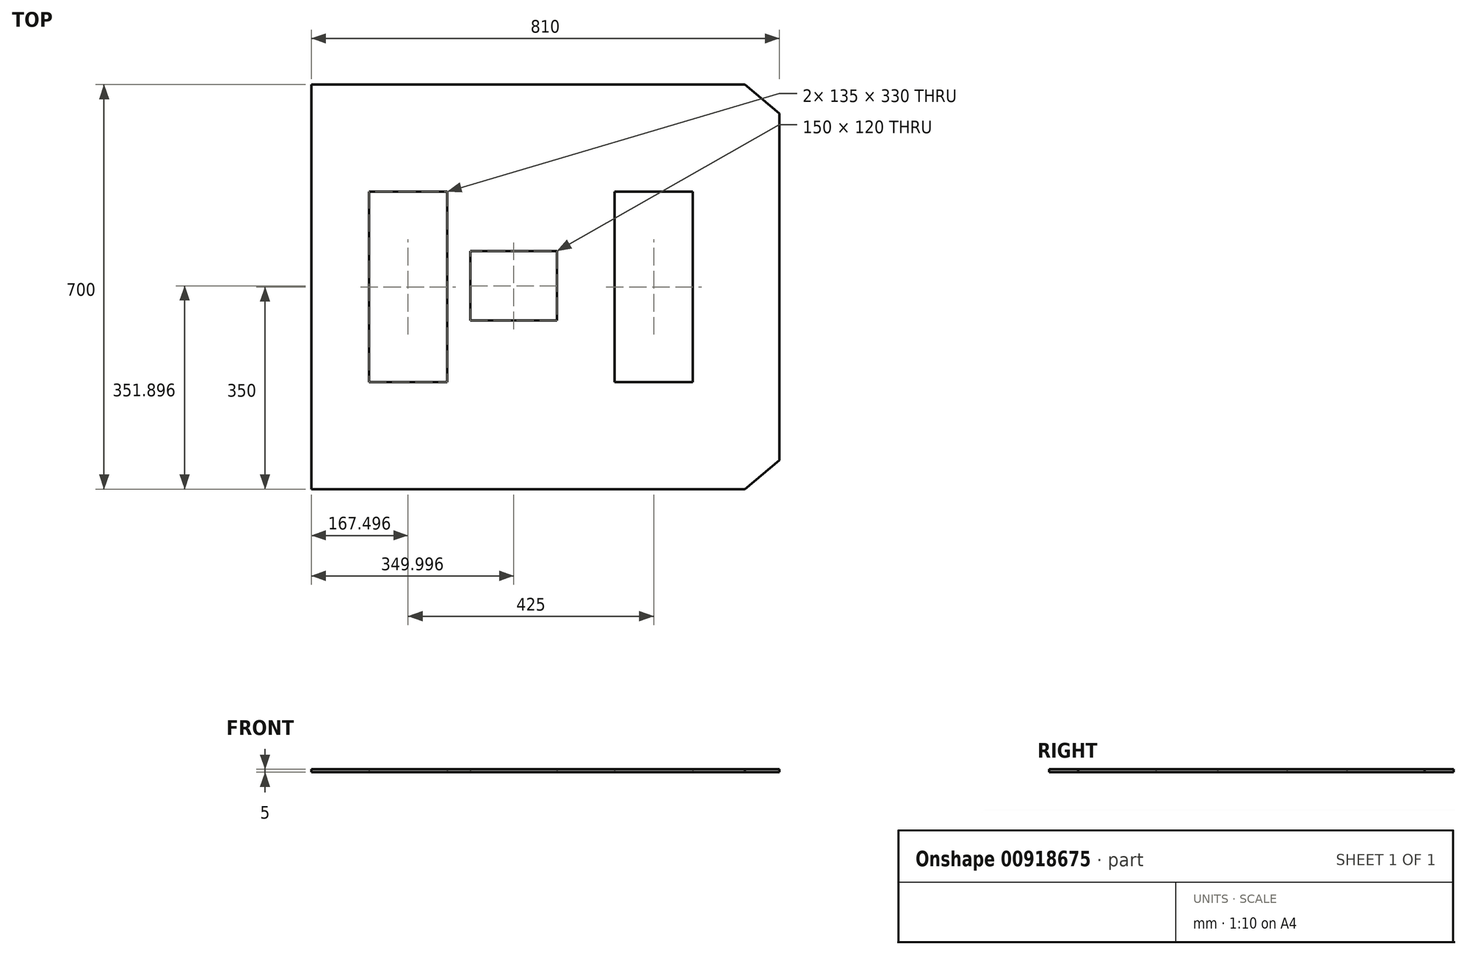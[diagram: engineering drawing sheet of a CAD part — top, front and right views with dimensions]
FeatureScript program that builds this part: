
annotation { "Feature Type Name" : "Feature", "Feature Type Description" : "" }
export const myFeature = defineFeature(function(context is Context, id is Id, definition is map)
    precondition{}
    {
        {
            var Q0;
            Q0=qCreatedBy(makeId("Front.planeOp"),FACE);
            var sketch = newSketch(context, id + "F0", { "sketchPlane" : qUnion([Q0])});
            skLineSegment(sketch, "E0", {"start": v(-514.8, 0) * mm, "end": v(635.2, 0) * mm, "construction": true});
            skLineSegment(sketch, "E1", {"start": v(-514.8, 0) * mm, "end": v(-514.8, 380) * mm, "construction": true});
            skCircle(sketch, "E2", {"center": v(-324.8, 190) * mm, "radius": 190 * mm, "construction": true});
            skPoint(sketch, "E2.first.point", {"position": v(-324.8, 0) * mm});
            skPoint(sketch, "E2.second.point", {"position": v(-514.8, 190) * mm});
            skPoint(sketch, "E2.third.point", {"position": v(-205.57, 337.94) * mm});
            skLineSegment(sketch, "E3", {"start": v(-514.8, 380) * mm, "end": v(635.2, 380) * mm, "construction": true});
            skLineSegment(sketch, "E4", {"start": v(635.2, 380) * mm, "end": v(635.2, 0) * mm, "construction": true});
            skCircle(sketch, "E5", {"center": v(445.2, 190) * mm, "radius": 190 * mm, "construction": true});
            skLineSegment(sketch, "E6", {"start": v(-134.8, 380) * mm, "end": v(-134.8, 0) * mm, "construction": true});
            skLineSegment(sketch, "E7", {"start": v(255.2, 380) * mm, "end": v(255.2, 0) * mm, "construction": true});
            skLineSegment(sketch, "E8", {"start": v(-542.2, 180) * mm, "end": v(670.63, 180) * mm, "construction": true});
            skLineSegment(sketch, "E9", {"start": v(-324.8, 408.83) * mm, "end": v(-324.8, -37.63) * mm, "construction": true});
            skLineSegment(sketch, "E10", {"start": v(445.2, 408.83) * mm, "end": v(445.2, -37.63) * mm, "construction": true});
            skLineSegment(sketch, "E11", {"start": v(294.65, 0) * mm, "end": v(294.65, 40) * mm, "construction": true});
            skLineSegment(sketch, "E12", {"start": v(294.65, 40) * mm, "end": v(635.2, 40) * mm, "construction": true});
            skSolve(sketch);
        }
        {
            var Q0;
            Q0=qCreatedBy(makeId("Top.planeOp"),FACE);
            var sketch = newSketch(context, id + "F1", { "sketchPlane" : qUnion([Q0])});
            skLineSegment(sketch, "E13", {"start": v(-514.8, 480) * mm, "end": v(-514.8, -480) * mm, "construction": true});
            skLineSegment(sketch, "E14", {"start": v(-134.8, 480) * mm, "end": v(-134.8, -480) * mm, "construction": true});
            skLineSegment(sketch, "E15", {"start": v(255.2, 480) * mm, "end": v(255.2, -480) * mm, "construction": true});
            skLineSegment(sketch, "E16", {"start": v(635.2, 480) * mm, "end": v(635.2, -480) * mm, "construction": true});
            skLineSegment(sketch, "E17", {"start": v(-514.8, 350) * mm, "end": v(125.2, 350) * mm, "construction": true});
            skLineSegment(sketch, "E18", {"start": v(-514.8, -350) * mm, "end": v(125.2, -350) * mm, "construction": true});
            skLineSegment(sketch, "E19", {"start": v(485.2, 180) * mm, "end": v(485.2, 0) * mm, "construction": true});
            skLineSegment(sketch, "E20", {"start": v(485.2, 0) * mm, "end": v(485.2, -180) * mm, "construction": true});
            skLineSegment(sketch, "E21", {"start": v(-514.8, 480) * mm, "end": v(635.2, 480) * mm, "construction": true});
            skLineSegment(sketch, "E22", {"start": v(-514.8, -480) * mm, "end": v(635.2, -480) * mm, "construction": true});
            skLineSegment(sketch, "E23", {"start": v(125.2, -350) * mm, "end": v(125.2, -350) * mm});
            skLineSegment(sketch, "E24", {"start": v(125.2, -350) * mm, "end": v(295.2, -350) * mm, "construction": true});
            skLineSegment(sketch, "E25", {"start": v(295.2, -350) * mm, "end": v(295.2, -235) * mm, "construction": true});
            skLineSegment(sketch, "E26", {"start": v(295.2, -235) * mm, "end": v(395.2, -235) * mm, "construction": true});
            skLineSegment(sketch, "E27", {"start": v(395.2, -235) * mm, "end": v(395.2, -180) * mm, "construction": true});
            skLineSegment(sketch, "E28", {"start": v(395.2, -180) * mm, "end": v(485.2, -180) * mm, "construction": true});
            skLineSegment(sketch, "E29", {"start": v(125.2, 350) * mm, "end": v(295.2, 350) * mm, "construction": true});
            skLineSegment(sketch, "E30.MirrorCS", {"start": v(125.2, 350) * mm, "end": v(125.2, 350) * mm});
            skLineSegment(sketch, "E31.MirrorCS", {"start": v(295.2, 350) * mm, "end": v(295.2, 235) * mm, "construction": true});
            skLineSegment(sketch, "E32.MirrorCS", {"start": v(295.2, 235) * mm, "end": v(395.2, 235) * mm, "construction": true});
            skLineSegment(sketch, "E33.MirrorCS", {"start": v(395.2, 235) * mm, "end": v(395.2, 180) * mm, "construction": true});
            skLineSegment(sketch, "E34.MirrorCS", {"start": v(395.2, 180) * mm, "end": v(485.2, 180) * mm, "construction": true});
            skLineSegment(sketch, "E35", {"start": v(295.2, 235) * mm, "end": v(295.2, -235) * mm, "construction": true});
            skSolve(sketch);
        }
        {
            var Q0;
            Q0=qCreatedBy(makeId("Front.planeOp"),FACE);
            var sketch = newSketch(context, id + "F2", { "sketchPlane" : qUnion([Q0])});
            skCircle(sketch, "E36", {"center": v(-214.8, 300) * mm, "radius": 300 * mm, "construction": true});
            skCircle(sketch, "E37", {"center": v(225.61, 60) * mm, "radius": 60 * mm, "construction": true});
            skLineSegment(sketch, "E38", {"start": v(225.61, 60) * mm, "end": v(485.39, 75) * mm, "construction": true});
            skLineSegment(sketch, "E39", {"start": v(485.39, 75) * mm, "end": v(485.39, 205.22) * mm, "construction": true});
            skLineSegment(sketch, "E40", {"start": v(485.39, 205.22) * mm, "end": v(333.21, 238.96) * mm, "construction": true});
            skLineSegment(sketch, "E41", {"start": v(333.21, 238.96) * mm, "end": v(289.28, 607.11) * mm, "construction": true});
            skLineSegment(sketch, "E42", {"start": v(289.28, 607.11) * mm, "end": v(240.41, 679.12) * mm, "construction": true});
            skLineSegment(sketch, "E43", {"start": v(240.41, 679.12) * mm, "end": v(-524.68, 643.12) * mm, "construction": true});
            skLineSegment(sketch, "E44", {"start": v(-219.79, 35) * mm, "end": v(-139.8, 35) * mm, "construction": true});
            skLineSegment(sketch, "E45", {"start": v(-179.8, 64.67) * mm, "end": v(-179.8, 16.9) * mm, "construction": true});
            skPoint(sketch, "E45.startSnap0", {"position": v(-179.8, 35) * mm});
            skLineSegment(sketch, "E46", {"start": v(-214.8, 300) * mm, "end": v(-214.8, 0) * mm, "construction": true});
            skLineSegment(sketch, "E47", {"start": v(-524.68, 643.12) * mm, "end": v(-510.83, 348.64) * mm});
            skSolve(sketch);
        }
        {
            var Q0;
            Q0=qCreatedBy(makeId("Top.planeOp"),FACE);
            var sketch = newSketch(context, id + "F3", { "sketchPlane" : qUnion([Q0])});
            skLineSegment(sketch, "E48", {"start": v(-514.8, 350) * mm, "end": v(135.2, 350) * mm, "construction": true});
            skLineSegment(sketch, "E49", {"start": v(-514.8, -350) * mm, "end": v(135.2, -350) * mm, "construction": true});
            skLineSegment(sketch, "E50", {"start": v(485.2, 180) * mm, "end": v(485.2, 0) * mm, "construction": true});
            skLineSegment(sketch, "E51", {"start": v(485.2, 0) * mm, "end": v(485.2, -180) * mm, "construction": true});
            skLineSegment(sketch, "E52", {"start": v(135.2, -350) * mm, "end": v(485.2, -284.96) * mm, "construction": true});
            skLineSegment(sketch, "E53", {"start": v(485.2, -284.96) * mm, "end": v(485.2, -180) * mm, "construction": true});
            skLineSegment(sketch, "E54", {"start": v(485.2, 180) * mm, "end": v(485.2, 284.96) * mm, "construction": true});
            skLineSegment(sketch, "E55", {"start": v(485.2, 284.96) * mm, "end": v(135.2, 350) * mm, "construction": true});
            skLineSegment(sketch, "E56", {"start": v(-514.8, 350) * mm, "end": v(-514.8, -350) * mm, "construction": true});
            skSolve(sketch);
        }
        {
            var Q0;
            Q0=qCreatedBy(makeId("Top.planeOp"),FACE);
            var sketch = newSketch(context, id + "F4", { "sketchPlane" : qUnion([Q0])});
            skLineSegment(sketch, "E57", {"start": v(125.2, 350) * mm, "end": v(125.2, 350) * mm});
            skLineSegment(sketch, "E58", {"start": v(295.2, 300) * mm, "end": v(295.2, -300) * mm});
            skLineSegment(sketch, "E59", {"start": v(235.2, -350) * mm, "end": v(-514.8, -350) * mm});
            skLineSegment(sketch, "E60", {"start": v(-514.8, -350) * mm, "end": v(-514.8, 350) * mm});
            skLineSegment(sketch, "E61.left", {"start": v(295.2, 235) * mm, "end": v(295.2, -235) * mm});
            skLineSegment(sketch, "E62", {"start": v(-514.8, 350) * mm, "end": v(235.2, 350) * mm});
            skPoint(sketch, "E63.orphan", {"position": v(295.2, 350) * mm});
            skLineSegment(sketch, "E64", {"start": v(235.2, 350) * mm, "end": v(295.2, 300) * mm});
            skLineSegment(sketch, "E65", {"start": v(295.2, -300) * mm, "end": v(235.2, -350) * mm});
            skPoint(sketch, "E66.end.orphan", {"position": v(-414.8, 150) * mm});
            skPoint(sketch, "E66.start.orphan", {"position": v(-514.8, 165) * mm});
            skPoint(sketch, "E67.end.orphan", {"position": v(-514.8, -165) * mm});
            skPoint(sketch, "E67.start.orphan", {"position": v(-414.8, -150) * mm});
            skLineSegment(sketch, "E68.bottom", {"start": v(-239.8, 61.9) * mm, "end": v(-89.8, 61.9) * mm});
            skLineSegment(sketch, "E68.top", {"start": v(-239.8, -58.1) * mm, "end": v(-89.8, -58.1) * mm});
            skLineSegment(sketch, "E68.left", {"start": v(-239.8, 61.9) * mm, "end": v(-239.8, -58.1) * mm});
            skLineSegment(sketch, "E68.right", {"start": v(-89.8, 61.9) * mm, "end": v(-89.8, -58.1) * mm});
            skPoint(sketch, "E69.orphan", {"position": v(-239.81, 61.9) * mm});
            skPoint(sketch, "E70.orphan", {"position": v(-239.81, -58.1) * mm});
            skPoint(sketch, "E71.right.start.orphan", {"position": v(145.2, 150) * mm});
            skPoint(sketch, "E71.left.start.orphan", {"position": v(-29.8, 150) * mm});
            skPoint(sketch, "E71.top.start.orphan", {"position": v(-29.8, -150) * mm});
            skPoint(sketch, "E72.trimOffspring.end.orphan", {"position": v(145.2, -150) * mm});
            skPoint(sketch, "E73.start.orphan", {"position": v(-279.8, 151.9) * mm});
            skPoint(sketch, "E74.start.orphan", {"position": v(-279.8, -148.1) * mm});
            skLineSegment(sketch, "E75.bottom", {"start": v(-414.8, 165) * mm, "end": v(-279.8, 165) * mm});
            skLineSegment(sketch, "E75.top", {"start": v(-414.8, -165) * mm, "end": v(-279.8, -165) * mm});
            skLineSegment(sketch, "E75.left", {"start": v(-414.8, 165) * mm, "end": v(-414.8, -165) * mm});
            skLineSegment(sketch, "E75.right", {"start": v(-279.8, 165) * mm, "end": v(-279.8, -165) * mm});
            skLineSegment(sketch, "E76.bottom", {"start": v(10.2, 165) * mm, "end": v(145.2, 165) * mm});
            skLineSegment(sketch, "E76.top", {"start": v(10.2, -165) * mm, "end": v(145.2, -165) * mm});
            skLineSegment(sketch, "E76.left", {"start": v(10.2, 165) * mm, "end": v(10.2, -165) * mm});
            skLineSegment(sketch, "E76.right", {"start": v(145.2, 165) * mm, "end": v(145.2, -165) * mm});
            skSolve(sketch);
        }
        {
            var Q0;
            {var subQ8=sQuery(id+"F4.wireOp",EDGE,"E59");Q0=makeQuery(id+"F4.imprint","IMPRINT",FACE,{"disambiguationData":[TD([[makeQuery(id+"F4.imprint","IMPRINT",EDGE,{"derivedFrom":subQ8}),-1.0]])]});}
            extrude(context, id + "F5", {"entities" : qUnion([Q0]), "depth" : 5 * mm, "offsetDistance" : 25.4 * mm});
        }
    });
